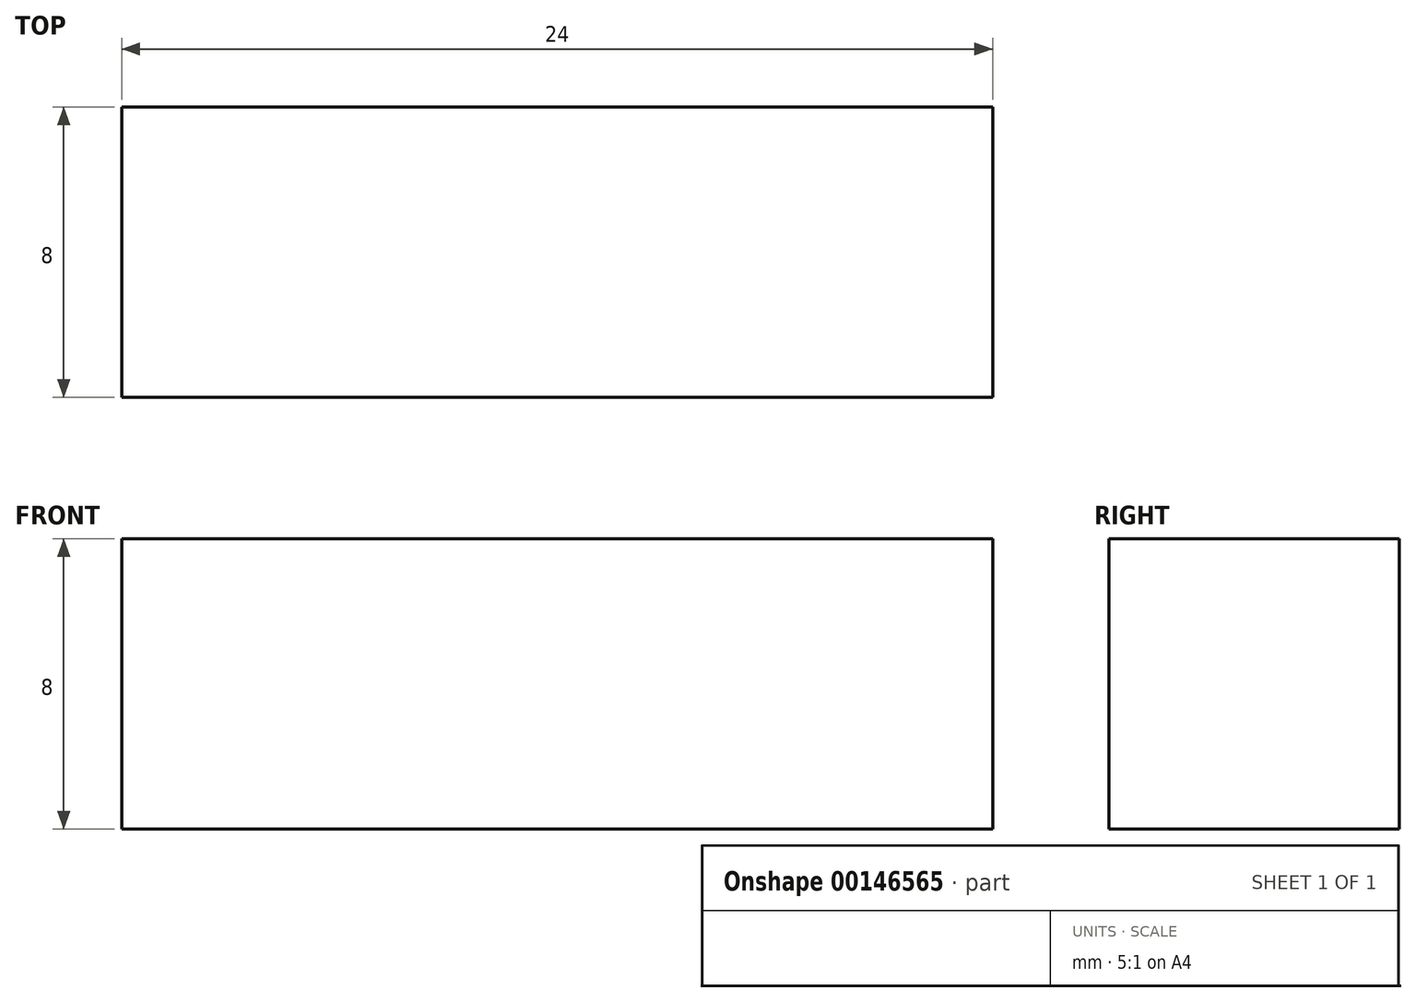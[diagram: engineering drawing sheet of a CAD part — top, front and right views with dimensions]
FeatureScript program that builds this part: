
annotation { "Feature Type Name" : "Feature", "Feature Type Description" : "" }
export const myFeature = defineFeature(function(context is Context, id is Id, definition is map)
    precondition{}
    {
        {
            assignVariable(context, id + "F0", {"name" : "width", "anyValue" : 8});
        }
        {
            var Q0;
            Q0=qCreatedBy(makeId("Front.planeOp"),FACE);
            var sketch = newSketch(context, id + "F1", { "sketchPlane" : qUnion([Q0])});
            skLineSegment(sketch, "E0", {"start": v(-12, 0) * mm, "end": v(-12, 8) * mm});
            skLineSegment(sketch, "E1", {"start": v(-12, 8) * mm, "end": v(12, 8) * mm});
            skLineSegment(sketch, "E2", {"start": v(12, 8) * mm, "end": v(12, 0) * mm});
            skLineSegment(sketch, "E3", {"start": v(12, 0) * mm, "end": v(-12, 0) * mm});
            skSolve(sketch);
        }
        {
            var Q0;
            Q0=makeQuery(id+"F1.imprint","IMPRINT",FACE,{"disambiguationData":[TD([[makeQuery(id+"F1.imprint","IMPRINT",EDGE,{"derivedFrom":sQuery(id+"F1.wireOp",EDGE,"E0")}),-1.0]])]});
            extrude(context, id + "F2", {"entities" : qUnion([Q0]), "depth" : (getVariable(context, 'width')) * mm, "symmetric" : true});
        }
    });
